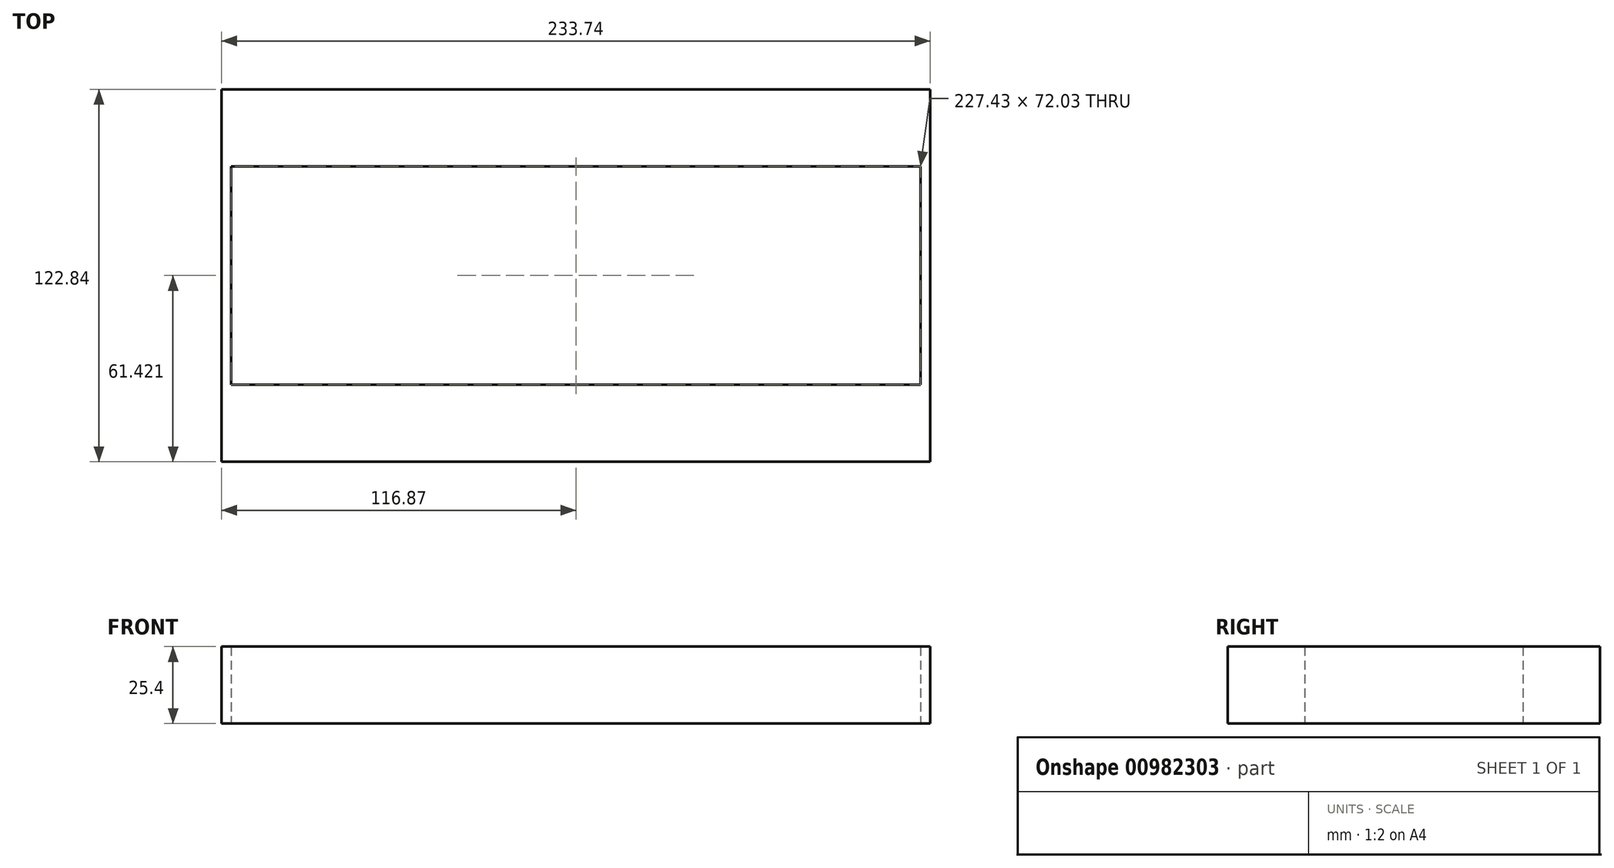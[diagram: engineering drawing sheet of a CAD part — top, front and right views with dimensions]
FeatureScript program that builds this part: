
annotation { "Feature Type Name" : "Feature", "Feature Type Description" : "" }
export const myFeature = defineFeature(function(context is Context, id is Id, definition is map)
    precondition{}
    {
        {
            var Q0;
            Q0=qCreatedBy(makeId("Top.planeOp"),FACE);
            var sketch = newSketch(context, id + "F0", { "sketchPlane" : qUnion([Q0])});
            skLineSegment(sketch, "E0.bottom", {"start": v(-110.57, 40.49) * mm, "end": v(116.87, 40.49) * mm});
            skLineSegment(sketch, "E0.top", {"start": v(-110.57, 15.09) * mm, "end": v(116.87, 15.09) * mm});
            skLineSegment(sketch, "E0.left", {"start": v(-110.57, 40.49) * mm, "end": v(-110.57, 15.09) * mm});
            skLineSegment(sketch, "E0.right", {"start": v(116.87, 40.49) * mm, "end": v(116.87, 15.09) * mm});
            skLineSegment(sketch, "E1.bottom", {"start": v(-110.57, -56.95) * mm, "end": v(116.87, -56.95) * mm});
            skLineSegment(sketch, "E1.top", {"start": v(-110.57, -82.35) * mm, "end": v(116.87, -82.35) * mm});
            skLineSegment(sketch, "E1.left", {"start": v(-110.57, -56.95) * mm, "end": v(-110.57, -82.35) * mm});
            skLineSegment(sketch, "E1.right", {"start": v(116.87, -56.95) * mm, "end": v(116.87, -82.35) * mm});
            skLineSegment(sketch, "E2.bottom", {"start": v(116.87, 40.49) * mm, "end": v(120.02, 40.49) * mm});
            skLineSegment(sketch, "E2.top", {"start": v(116.87, -82.35) * mm, "end": v(120.02, -82.35) * mm});
            skLineSegment(sketch, "E2.left", {"start": v(116.87, 40.49) * mm, "end": v(116.87, -82.35) * mm});
            skLineSegment(sketch, "E2.right", {"start": v(120.02, 40.49) * mm, "end": v(120.02, -82.35) * mm});
            skPoint(sketch, "E3.oppositeSnap0", {"position": v(118.44, -82.35) * mm});
            skLineSegment(sketch, "E3.bottom", {"start": v(-110.57, 40.49) * mm, "end": v(-113.72, 40.49) * mm});
            skLineSegment(sketch, "E3.top", {"start": v(-110.57, -82.35) * mm, "end": v(-113.72, -82.35) * mm});
            skLineSegment(sketch, "E3.left", {"start": v(-110.57, 40.49) * mm, "end": v(-110.57, -82.35) * mm});
            skLineSegment(sketch, "E3.right", {"start": v(-113.72, 40.49) * mm, "end": v(-113.72, -82.35) * mm});
            skPoint(sketch, "E4.firstSnap0", {"position": v(3.15, 15.09) * mm});
            skLineSegment(sketch, "E4.bottom", {"start": v(0, 15.09) * mm, "end": v(3.15, 15.09) * mm});
            skLineSegment(sketch, "E4.top", {"start": v(0, -56.95) * mm, "end": v(3.15, -56.95) * mm});
            skLineSegment(sketch, "E4.left", {"start": v(0, 15.09) * mm, "end": v(0, -56.95) * mm});
            skLineSegment(sketch, "E4.right", {"start": v(3.15, 15.09) * mm, "end": v(3.15, -56.95) * mm});
            skSolve(sketch);
        }
        {
            var Q0;
            {var subQ1=sQuery(id+"F0.wireOp",EDGE,"E0.bottom");Q0=makeQuery(id+"F0.imprint","IMPRINT",FACE,{"disambiguationData":[TD([[makeQuery(id+"F0.imprint","IMPRINT",EDGE,{"derivedFrom":subQ1}),-1.0]])]});}
            var Q1;
            {var subQ3=sQuery(id+"F0.wireOp",EDGE,"E1.top");Q1=makeQuery(id+"F0.imprint","IMPRINT",FACE,{"disambiguationData":[TD([[makeQuery(id+"F0.imprint","IMPRINT",EDGE,{"derivedFrom":subQ3}),1.0]])]});}
            var Q2;
            {var subQ3=sQuery(id+"F0.wireOp",EDGE,"E3.bottom");Q2=makeQuery(id+"F0.imprint","IMPRINT",FACE,{"disambiguationData":[TD([[makeQuery(id+"F0.imprint","IMPRINT",EDGE,{"derivedFrom":subQ3}),1.0]])]});}
            var Q3;
            Q3=makeQuery(id+"F0.imprint","IMPRINT",FACE,{"disambiguationData":[TD([[makeQuery(id+"F0.imprint","IMPRINT",EDGE,{"derivedFrom":sQuery(id+"F0.wireOp",EDGE,"E4.bottom")}),-1.0]])]});
            var Q4;
            {var subQ3=sQuery(id+"F0.wireOp",EDGE,"E2.bottom");Q4=makeQuery(id+"F0.imprint","IMPRINT",FACE,{"disambiguationData":[TD([[makeQuery(id+"F0.imprint","IMPRINT",EDGE,{"derivedFrom":subQ3}),-1.0]])]});}
            extrude(context, id + "F1", {"entities" : qUnion([Q0, Q1, Q2, Q3, Q4]), "depth" : 25.4 * mm, "offsetDistance" : 25.4 * mm});
        }
    });
